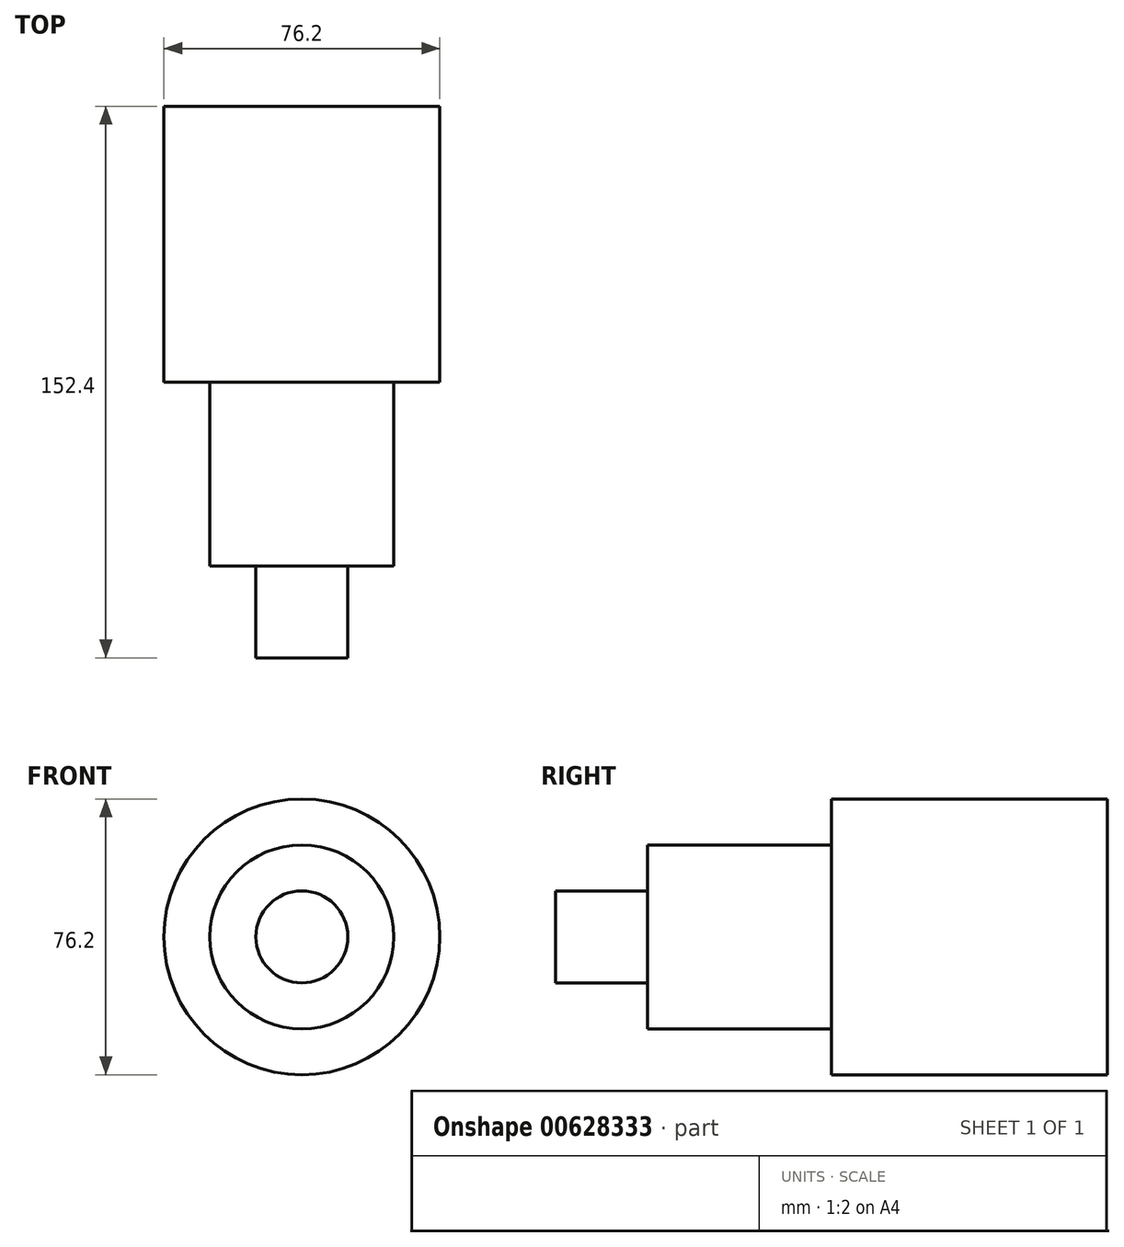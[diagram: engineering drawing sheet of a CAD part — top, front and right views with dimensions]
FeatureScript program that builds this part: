
annotation { "Feature Type Name" : "Feature", "Feature Type Description" : "" }
export const myFeature = defineFeature(function(context is Context, id is Id, definition is map)
    precondition{}
    {
        {
            var Q0;
            Q0=qCreatedBy(makeId("Front.planeOp"),FACE);
            var sketch = newSketch(context, id + "F0", { "sketchPlane" : qUnion([Q0])});
            skCircle(sketch, "E0", {"center": v(0, 0) * mm, "radius": 38.1 * mm});
            skCircle(sketch, "E1", {"center": v(0, 0) * mm, "radius": 25.4 * mm});
            skCircle(sketch, "E2", {"center": v(0, 0) * mm, "radius": 12.7 * mm});
            skSolve(sketch);
        }
        {
            var Q0;
            Q0=makeQuery(id+"F0.imprint","IMPRINT",FACE,{"disambiguationData":[TD([[makeQuery(id+"F0.imprint","IMPRINT",EDGE,{"derivedFrom":sQuery(id+"F0.wireOp",EDGE,"E0")}),1.0]])]});
            extrude(context, id + "F1", {"entities" : qUnion([Q0]), "depth" : 76.2 * mm, "offsetDistance" : 25.4 * mm});
        }
        {
            var Q0;
            Q0=makeQuery(id+"F0.imprint","IMPRINT",FACE,{"disambiguationData":[TD([[makeQuery(id+"F0.imprint","IMPRINT",EDGE,{"derivedFrom":sQuery(id+"F0.wireOp",EDGE,"E1")}),1.0]])]});
            extrude(context, id + "F2", {"entities" : qUnion([Q0]), "operationType" : NewBodyOperationType.ADD, "depth" : 127 * mm, "offsetDistance" : 25.4 * mm});
        }
        {
            var Q0;
            Q0=makeQuery(id+"F0.imprint","IMPRINT",FACE,{"disambiguationData":[TD([[makeQuery(id+"F0.imprint","IMPRINT",EDGE,{"derivedFrom":sQuery(id+"F0.wireOp",EDGE,"E2")}),1.0]])]});
            extrude(context, id + "F3", {"entities" : qUnion([Q0]), "operationType" : NewBodyOperationType.ADD, "depth" : 152.4 * mm, "offsetDistance" : 25.4 * mm});
        }
    });
